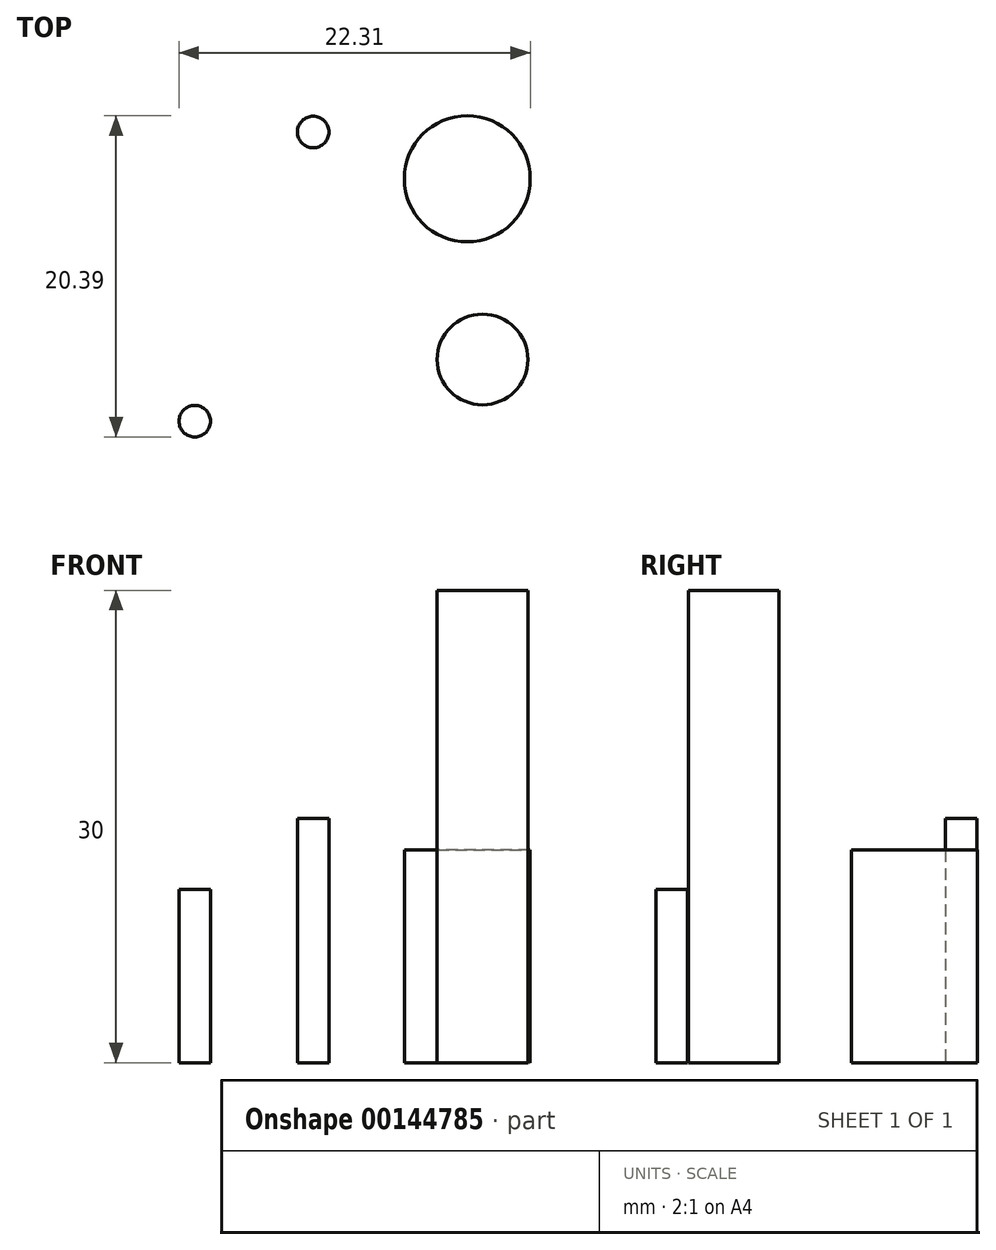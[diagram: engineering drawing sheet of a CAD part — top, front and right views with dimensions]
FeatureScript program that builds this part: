
annotation { "Feature Type Name" : "Feature", "Feature Type Description" : "" }
export const myFeature = defineFeature(function(context is Context, id is Id, definition is map)
    precondition{}
    {
        {
            var Q0;
            Q0=qCreatedBy(makeId("Top.planeOp"),FACE);
            var sketch = newSketch(context, id + "F0", { "sketchPlane" : qUnion([Q0])});
            skCircle(sketch, "E0", {"center": v(-46, 25.1) * mm, "radius": 1 * mm});
            skCircle(sketch, "E1", {"center": v(-36.2, 22.13) * mm, "radius": 4 * mm});
            skCircle(sketch, "E2", {"center": v(-53.52, 6.73) * mm, "radius": 1 * mm});
            skCircle(sketch, "E3", {"center": v(-35.24, 10.66) * mm, "radius": 2.88 * mm});
            skSolve(sketch);
        }
        {
            var Q0;
            Q0=makeQuery(id+"F0.imprint","IMPRINT",FACE,{"disambiguationData":[TD([[makeQuery(id+"F0.imprint","IMPRINT",EDGE,{"derivedFrom":sQuery(id+"F0.wireOp",EDGE,"E1")}),1.0]])]});
            extrude(context, id + "F1", {"entities" : qUnion([Q0]), "depth" : 13.5 * mm});
        }
        {
            var Q0;
            Q0=makeQuery(id+"F0.imprint","IMPRINT",FACE,{"disambiguationData":[TD([[makeQuery(id+"F0.imprint","IMPRINT",EDGE,{"derivedFrom":sQuery(id+"F0.wireOp",EDGE,"E0")}),1.0]])]});
            extrude(context, id + "F2", {"entities" : qUnion([Q0]), "depth" : 15.5 * mm});
        }
        {
            var Q0;
            Q0=makeQuery(id+"F0.imprint","IMPRINT",FACE,{"disambiguationData":[TD([[makeQuery(id+"F0.imprint","IMPRINT",EDGE,{"derivedFrom":sQuery(id+"F0.wireOp",EDGE,"E2")}),1.0]])]});
            var Q1;
            Q1=sQuery(id+"F0.wireOp",EDGE,"E2");
            extrude(context, id + "F3", {"entities" : qUnion([Q0]), "surfaceEntities" : qUnion([Q1]), "depth" : 11 * mm});
        }
        {
            var Q0;
            Q0=makeQuery(id+"F0.imprint","IMPRINT",FACE,{"disambiguationData":[TD([[makeQuery(id+"F0.imprint","IMPRINT",EDGE,{"derivedFrom":sQuery(id+"F0.wireOp",EDGE,"E3")}),1.0]])]});
            extrude(context, id + "F4", {"entities" : qUnion([Q0]), "depth" : 30 * mm});
        }
    });
